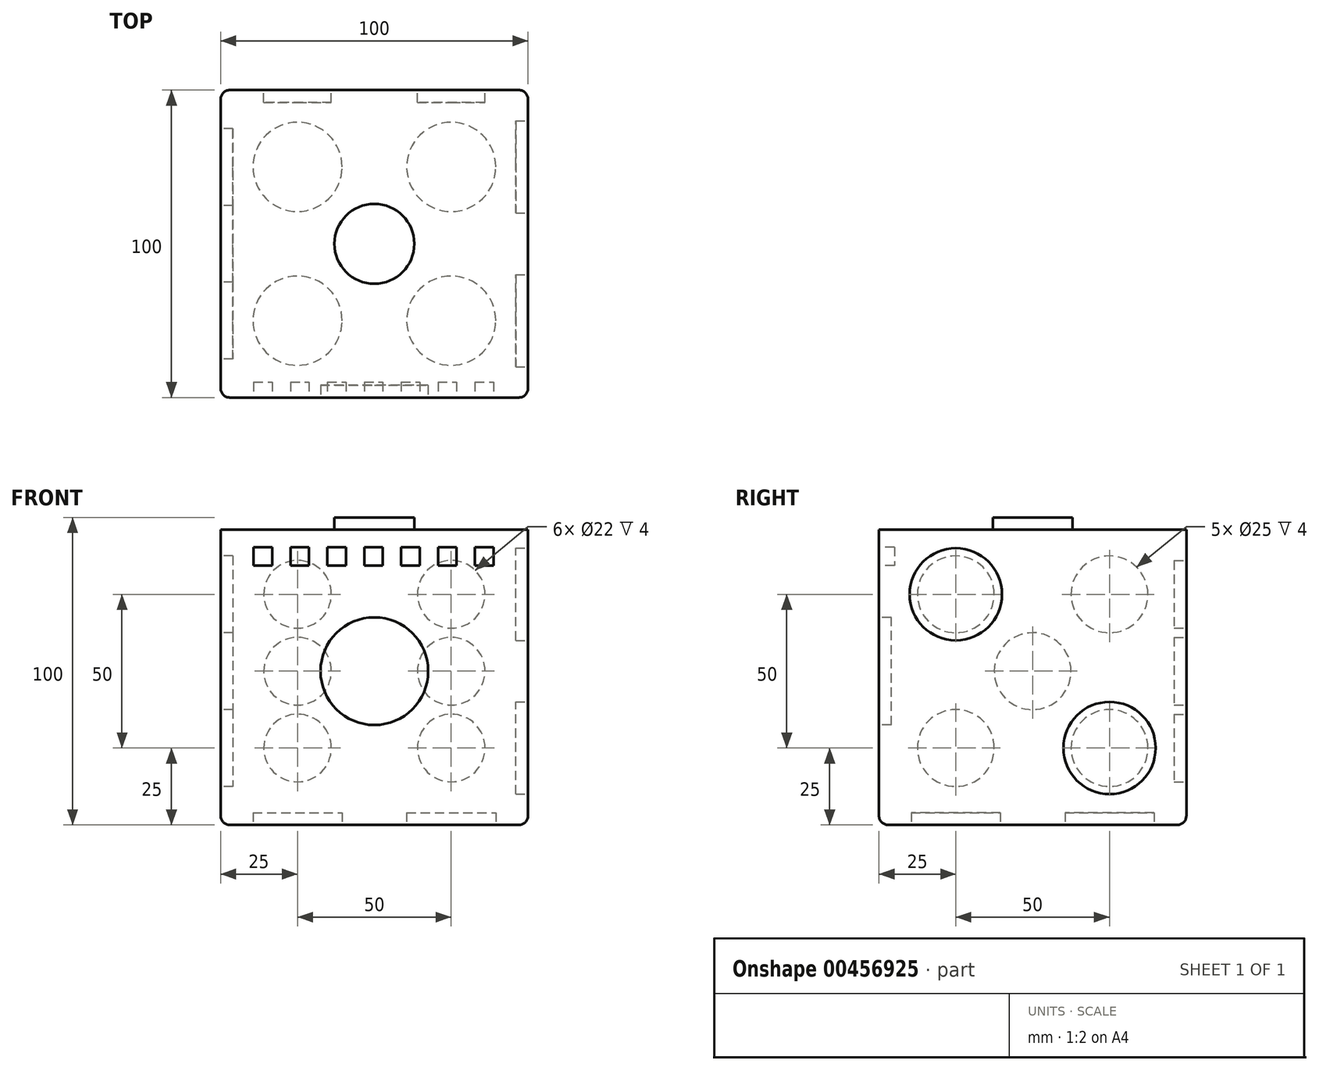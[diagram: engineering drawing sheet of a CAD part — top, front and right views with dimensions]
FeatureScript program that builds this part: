
annotation { "Feature Type Name" : "Feature", "Feature Type Description" : "" }
export const myFeature = defineFeature(function(context is Context, id is Id, definition is map)
    precondition{}
    {
        {
            var Q0;
            Q0=qCreatedBy(makeId("Top.planeOp"),FACE);
            var sketch = newSketch(context, id + "F0", { "sketchPlane" : qUnion([Q0])});
            skLineSegment(sketch, "E0.bottom", {"start": v(50, -50) * mm, "end": v(-50, -50) * mm});
            skLineSegment(sketch, "E0.top", {"start": v(50, 50) * mm, "end": v(-50, 50) * mm});
            skLineSegment(sketch, "E0.left", {"start": v(50, -50) * mm, "end": v(50, 50) * mm});
            skLineSegment(sketch, "E0.right", {"start": v(-50, -50) * mm, "end": v(-50, 50) * mm});
            skPoint(sketch, "E0.middle", {"position": v(0, 0) * mm});
            skSolve(sketch);
        }
        {
            var Q0;
            Q0 = qSketchRegion(id + "F0", true);
            extrude(context, id + "F1", {"entities" : qUnion([Q0]), "endBound" : BoundingType.SYMMETRIC, "depth" : 100 * mm});
        }
        {
            var Q0;
            Q0=makeQuery(id+"F1.opExtrude","SWEPT_FACE",FACE,{"disambiguationData":[OSD([sQuery(id+"F0.wireOp",EDGE,"E0.bottom")])]});
            var sketch = newSketch(context, id + "F2", { "sketchPlane" : qUnion([Q0])});
            skCircle(sketch, "E1", {"center": v(0, 0) * mm, "radius": 17.5 * mm});
            skSolve(sketch);
        }
        {
            var Q0;
            Q0=makeQuery(id+"F2.imprint","IMPRINT",FACE,{"disambiguationData":[TD([[makeQuery(id+"F2.imprint","IMPRINT",EDGE,{"derivedFrom":sQuery(id+"F2.wireOp",EDGE,"E1")}),1.0]])]});
            extrude(context, id + "F3", {"entities" : qUnion([Q0]), "operationType" : NewBodyOperationType.REMOVE, "oppositeDirection" : true, "depth" : 4 * mm});
        }
        {
            var Q0;
            Q0=makeQuery(id+"F1.opExtrude","SWEPT_FACE",FACE,{"disambiguationData":[OSD([sQuery(id+"F0.wireOp",EDGE,"E0.left")])]});
            var sketch = newSketch(context, id + "F4", { "sketchPlane" : qUnion([Q0])});
            skCircle(sketch, "E2", {"center": v(-25, 25) * mm, "radius": 15 * mm});
            skCircle(sketch, "E3", {"center": v(25, -25) * mm, "radius": 15 * mm});
            skSolve(sketch);
        }
        {
            var Q0;
            Q0=makeQuery(id+"F4.imprint","IMPRINT",FACE,{"disambiguationData":[TD([[makeQuery(id+"F4.imprint","IMPRINT",EDGE,{"derivedFrom":sQuery(id+"F4.wireOp",EDGE,"E2")}),1.0]])]});
            var Q1;
            Q1=makeQuery(id+"F4.imprint","IMPRINT",FACE,{"disambiguationData":[TD([[makeQuery(id+"F4.imprint","IMPRINT",EDGE,{"derivedFrom":sQuery(id+"F4.wireOp",EDGE,"E3")}),1.0]])]});
            extrude(context, id + "F5", {"entities" : qUnion([Q0, Q1]), "operationType" : NewBodyOperationType.REMOVE, "oppositeDirection" : true, "depth" : 4 * mm});
        }
        {
            var Q0;
            Q0=makeQuery(id+"F1.opExtrude","CAP_FACE",FACE,{"disambiguationData":[OSD([sQuery(id+"F0.wireOp",EDGE,"E0.bottom"),sQuery(id+"F0.wireOp",EDGE,"E0.top"),sQuery(id+"F0.wireOp",EDGE,"E0.left"),sQuery(id+"F0.wireOp",EDGE,"E0.right")])],"isStart":false});
            var sketch = newSketch(context, id + "F6", { "sketchPlane" : qUnion([Q0])});
            skLineSegment(sketch, "E4", {"start": v(-50, 0) * mm, "end": v(50, 0) * mm});
            skCircle(sketch, "E5", {"center": v(-25, 25) * mm, "radius": 13 * mm});
            skCircle(sketch, "E6", {"center": v(0, 0) * mm, "radius": 13 * mm});
            skCircle(sketch, "E7", {"center": v(25, -25) * mm, "radius": 13 * mm});
            skSolve(sketch);
        }
        {
            var Q0;
            Q0=makeQuery(id+"F6.imprint","IMPRINT",FACE,{"disambiguationData":[TD([[makeQuery(id+"F6.imprint","IMPRINT",EDGE,{"derivedFrom":sQuery(id+"F6.wireOp",EDGE,"E5")}),1.0]])]});
            var Q1;
            {var subQ0=sQuery(id+"F6.wireOp",EDGE,"E6");var subQ1=sQuery(id+"F6.wireOp",EDGE,"E4");var subQ2=makeQuery(id+"F6.imprint","INTERSECT",VERTEX,{"disambiguationData":[OD(0.0)],"derivedFrom":[subQ1,subQ0]});Q1=makeQuery(id+"F6.imprint","IMPRINT",FACE,{"disambiguationData":[TD([[makeQuery(id+"F6.imprint","IMPRINT",EDGE,{"disambiguationData":[TD([[subQ2,-1.0]])],"derivedFrom":subQ1}),1.0]])]});}
            var Q2;
            {var subQ0=sQuery(id+"F6.wireOp",EDGE,"E6");var subQ1=sQuery(id+"F6.wireOp",EDGE,"E4");var subQ2=makeQuery(id+"F6.imprint","INTERSECT",VERTEX,{"disambiguationData":[OD(0.0)],"derivedFrom":[subQ1,subQ0]});Q2=makeQuery(id+"F6.imprint","IMPRINT",FACE,{"disambiguationData":[TD([[makeQuery(id+"F6.imprint","IMPRINT",EDGE,{"disambiguationData":[TD([[subQ2,-1.0]])],"derivedFrom":subQ1}),-1.0]])]});}
            var Q3;
            Q3=makeQuery(id+"F6.imprint","IMPRINT",FACE,{"disambiguationData":[TD([[makeQuery(id+"F6.imprint","IMPRINT",EDGE,{"derivedFrom":sQuery(id+"F6.wireOp",EDGE,"E7")}),1.0]])]});
            extrude(context, id + "F7", {"entities" : qUnion([Q0, Q1, Q2, Q3]), "operationType" : NewBodyOperationType.REMOVE, "oppositeDirection" : true, "depth" : 4 * mm});
        }
        {
            var Q0;
            Q0=makeQuery(id+"F1.opExtrude","CAP_FACE",FACE,{"disambiguationData":[OSD([sQuery(id+"F0.wireOp",EDGE,"E0.bottom"),sQuery(id+"F0.wireOp",EDGE,"E0.top"),sQuery(id+"F0.wireOp",EDGE,"E0.left"),sQuery(id+"F0.wireOp",EDGE,"E0.right")])],"isStart":true});
            var sketch = newSketch(context, id + "F8", { "sketchPlane" : qUnion([Q0])});
            skCircle(sketch, "E8", {"center": v(-25, -25) * mm, "radius": 14.5 * mm});
            skCircle(sketch, "E9", {"center": v(25, -25) * mm, "radius": 14.5 * mm});
            skCircle(sketch, "E10", {"center": v(25, 25) * mm, "radius": 14.5 * mm});
            skCircle(sketch, "E11", {"center": v(-25, 25) * mm, "radius": 14.5 * mm});
            skSolve(sketch);
        }
        {
            var Q0;
            Q0=makeQuery(id+"F8.imprint","IMPRINT",FACE,{"disambiguationData":[TD([[makeQuery(id+"F8.imprint","IMPRINT",EDGE,{"derivedFrom":sQuery(id+"F8.wireOp",EDGE,"E11")}),1.0]])]});
            var Q1;
            Q1=makeQuery(id+"F8.imprint","IMPRINT",FACE,{"disambiguationData":[TD([[makeQuery(id+"F8.imprint","IMPRINT",EDGE,{"derivedFrom":sQuery(id+"F8.wireOp",EDGE,"E10")}),1.0]])]});
            var Q2;
            Q2=makeQuery(id+"F8.imprint","IMPRINT",FACE,{"disambiguationData":[TD([[makeQuery(id+"F8.imprint","IMPRINT",EDGE,{"derivedFrom":sQuery(id+"F8.wireOp",EDGE,"E8")}),1.0]])]});
            var Q3;
            Q3=makeQuery(id+"F8.imprint","IMPRINT",FACE,{"disambiguationData":[TD([[makeQuery(id+"F8.imprint","IMPRINT",EDGE,{"derivedFrom":sQuery(id+"F8.wireOp",EDGE,"E9")}),1.0]])]});
            extrude(context, id + "F9", {"entities" : qUnion([Q0, Q1, Q2, Q3]), "operationType" : NewBodyOperationType.REMOVE, "oppositeDirection" : true, "depth" : 4 * mm});
        }
        {
            var Q0;
            Q0=makeQuery(id+"F1.opExtrude","SWEPT_FACE",FACE,{"disambiguationData":[OSD([sQuery(id+"F0.wireOp",EDGE,"E0.right")])]});
            var sketch = newSketch(context, id + "F10", { "sketchPlane" : qUnion([Q0])});
            skCircle(sketch, "E12", {"center": v(0, 0) * mm, "radius": 12.5 * mm});
            skCircle(sketch, "E13", {"center": v(25, 25) * mm, "radius": 12.5 * mm});
            skCircle(sketch, "E14", {"center": v(-25, 25) * mm, "radius": 12.5 * mm});
            skCircle(sketch, "E15", {"center": v(-25, -25) * mm, "radius": 12.5 * mm});
            skCircle(sketch, "E16", {"center": v(25, -25) * mm, "radius": 12.5 * mm});
            skSolve(sketch);
        }
        {
            var Q0;
            Q0 = qSketchRegion(id + "F10", true);
            extrude(context, id + "F11", {"entities" : qUnion([Q0]), "operationType" : NewBodyOperationType.REMOVE, "oppositeDirection" : true, "depth" : 4 * mm});
        }
        {
            var Q0;
            Q0=makeQuery(id+"F1.opExtrude","SWEPT_FACE",FACE,{"disambiguationData":[OSD([sQuery(id+"F0.wireOp",EDGE,"E0.top")])]});
            var sketch = newSketch(context, id + "F12", { "sketchPlane" : qUnion([Q0])});
            skCircle(sketch, "E17", {"center": v(-25, 0) * mm, "radius": 11 * mm});
            skCircle(sketch, "E18", {"center": v(-25, 25) * mm, "radius": 11 * mm});
            skCircle(sketch, "E19", {"center": v(-25, -25) * mm, "radius": 11 * mm});
            skCircle(sketch, "E20", {"center": v(25, -25) * mm, "radius": 11 * mm});
            skCircle(sketch, "E21", {"center": v(25, 0) * mm, "radius": 11 * mm});
            skCircle(sketch, "E22", {"center": v(25, 25) * mm, "radius": 11 * mm});
            skSolve(sketch);
        }
        {
            var Q0;
            Q0 = qSketchRegion(id + "F12", true);
            extrude(context, id + "F13", {"entities" : qUnion([Q0]), "operationType" : NewBodyOperationType.REMOVE, "oppositeDirection" : true, "depth" : 4 * mm});
        }
        {
            var Q0;
            Q0=makeQuery(id+"F1.opExtrude","CAP_EDGE",EDGE,{"disambiguationData":[OSD([sQuery(id+"F0.wireOp",EDGE,"E0.left")])],"isStart":false});
            var Q1;
            Q1=makeQuery(id+"F1.opExtrude","CAP_EDGE",EDGE,{"disambiguationData":[OSD([sQuery(id+"F0.wireOp",EDGE,"E0.top")])],"isStart":false});
            var Q2;
            Q2=makeQuery(id+"F1.opExtrude","CAP_EDGE",EDGE,{"disambiguationData":[OSD([sQuery(id+"F0.wireOp",EDGE,"E0.right")])],"isStart":false});
            var Q3;
            Q3=makeQuery(id+"F1.opExtrude","CAP_EDGE",EDGE,{"disambiguationData":[OSD([sQuery(id+"F0.wireOp",EDGE,"E0.bottom")])],"isStart":false});
            var Q4;
            Q4=makeQuery(id+"F1.opExtrude","SWEPT_EDGE",EDGE,{"disambiguationData":[OSD([sQuery(id+"F0.wireOp",EDGE,"E0.bottom"),sQuery(id+"F0.wireOp",EDGE,"E0.right")])]});
            var Q5;
            Q5=makeQuery(id+"F1.opExtrude","CAP_EDGE",EDGE,{"disambiguationData":[OSD([sQuery(id+"F0.wireOp",EDGE,"E0.bottom")])],"isStart":true});
            var Q6;
            Q6=makeQuery(id+"F1.opExtrude","SWEPT_EDGE",EDGE,{"disambiguationData":[OSD([sQuery(id+"F0.wireOp",EDGE,"E0.bottom"),sQuery(id+"F0.wireOp",EDGE,"E0.left")])]});
            var Q7;
            Q7=makeQuery(id+"F1.opExtrude","CAP_EDGE",EDGE,{"disambiguationData":[OSD([sQuery(id+"F0.wireOp",EDGE,"E0.left")])],"isStart":true});
            var Q8;
            Q8=makeQuery(id+"F1.opExtrude","CAP_EDGE",EDGE,{"disambiguationData":[OSD([sQuery(id+"F0.wireOp",EDGE,"E0.top")])],"isStart":true});
            var Q9;
            Q9=makeQuery(id+"F1.opExtrude","SWEPT_EDGE",EDGE,{"disambiguationData":[OSD([sQuery(id+"F0.wireOp",EDGE,"E0.top"),sQuery(id+"F0.wireOp",EDGE,"E0.left")])]});
            var Q10;
            Q10=makeQuery(id+"F1.opExtrude","SWEPT_EDGE",EDGE,{"disambiguationData":[OSD([sQuery(id+"F0.wireOp",EDGE,"E0.top"),sQuery(id+"F0.wireOp",EDGE,"E0.right")])]});
            var Q11;
            Q11=makeQuery(id+"F1.opExtrude","CAP_EDGE",EDGE,{"disambiguationData":[OSD([sQuery(id+"F0.wireOp",EDGE,"E0.right")])],"isStart":true});
            fillet(context, id + "F14", {"entities" : qUnion([Q0, Q1, Q2, Q3, Q4, Q5, Q6, Q7, Q8, Q9, Q10, Q11]), "radius" : 3 * mm, "tangentPropagation" : true, "allowEdgeOverflow" : false});
        }
        {
            var Q0;
            Q0=makeQuery(id+"F1.opExtrude","SWEPT_FACE",FACE,{"disambiguationData":[OSD([sQuery(id+"F0.wireOp",EDGE,"E0.bottom")])]});
            var sketch = newSketch(context, id + "F15", { "sketchPlane" : qUnion([Q0])});
            skLineSegment(sketch, "E23.bottom", {"start": v(-39.26, 40.35) * mm, "end": v(-33.26, 40.35) * mm});
            skLineSegment(sketch, "E23.top", {"start": v(-39.26, 34.35) * mm, "end": v(-33.26, 34.35) * mm});
            skLineSegment(sketch, "E23.left", {"start": v(-39.26, 40.35) * mm, "end": v(-39.26, 34.35) * mm});
            skLineSegment(sketch, "E23.right", {"start": v(-33.26, 40.35) * mm, "end": v(-33.26, 34.35) * mm});
            skLineSegment(sketch, "E24.1.0.0", {"start": v(-27.26, 40.35) * mm, "end": v(-21.26, 40.35) * mm});
            skLineSegment(sketch, "E24.1.0.1", {"start": v(-21.26, 40.35) * mm, "end": v(-21.26, 34.35) * mm});
            skLineSegment(sketch, "E24.1.0.2", {"start": v(-27.26, 34.35) * mm, "end": v(-21.26, 34.35) * mm});
            skLineSegment(sketch, "E24.1.0.3", {"start": v(-27.26, 40.35) * mm, "end": v(-27.26, 34.35) * mm});
            skLineSegment(sketch, "E24.2.0.0", {"start": v(-15.26, 40.35) * mm, "end": v(-9.26, 40.35) * mm});
            skLineSegment(sketch, "E24.2.0.1", {"start": v(-9.26, 40.35) * mm, "end": v(-9.26, 34.35) * mm});
            skLineSegment(sketch, "E24.2.0.2", {"start": v(-15.26, 34.35) * mm, "end": v(-9.26, 34.35) * mm});
            skLineSegment(sketch, "E24.2.0.3", {"start": v(-15.26, 40.35) * mm, "end": v(-15.26, 34.35) * mm});
            skLineSegment(sketch, "E24.direction1", {"start": v(-39.26, 34.35) * mm, "end": v(-27.26, 34.35) * mm, "construction": true});
            skLineSegment(sketch, "E25.0.3.0", {"start": v(-3.26, 40.35) * mm, "end": v(2.74, 40.35) * mm});
            skLineSegment(sketch, "E25.3.3.0", {"start": v(2.74, 40.35) * mm, "end": v(2.74, 34.35) * mm});
            skLineSegment(sketch, "E25.6.3.0", {"start": v(-3.26, 34.35) * mm, "end": v(2.74, 34.35) * mm});
            skLineSegment(sketch, "E25.9.3.0", {"start": v(-3.26, 40.35) * mm, "end": v(-3.26, 34.35) * mm});
            skLineSegment(sketch, "E25.0.4.0", {"start": v(8.74, 40.35) * mm, "end": v(14.74, 40.35) * mm});
            skLineSegment(sketch, "E25.3.4.0", {"start": v(14.74, 40.35) * mm, "end": v(14.74, 34.35) * mm});
            skLineSegment(sketch, "E25.6.4.0", {"start": v(8.74, 34.35) * mm, "end": v(14.74, 34.35) * mm});
            skLineSegment(sketch, "E25.9.4.0", {"start": v(8.74, 40.35) * mm, "end": v(8.74, 34.35) * mm});
            skLineSegment(sketch, "E25.0.5.0", {"start": v(20.74, 40.35) * mm, "end": v(26.74, 40.35) * mm});
            skLineSegment(sketch, "E25.3.5.0", {"start": v(26.74, 40.35) * mm, "end": v(26.74, 34.35) * mm});
            skLineSegment(sketch, "E25.6.5.0", {"start": v(20.74, 34.35) * mm, "end": v(26.74, 34.35) * mm});
            skLineSegment(sketch, "E25.9.5.0", {"start": v(20.74, 40.35) * mm, "end": v(20.74, 34.35) * mm});
            skLineSegment(sketch, "E25.0.6.0", {"start": v(32.74, 40.35) * mm, "end": v(38.74, 40.35) * mm});
            skLineSegment(sketch, "E25.3.6.0", {"start": v(38.74, 40.35) * mm, "end": v(38.74, 34.35) * mm});
            skLineSegment(sketch, "E25.6.6.0", {"start": v(32.74, 34.35) * mm, "end": v(38.74, 34.35) * mm});
            skLineSegment(sketch, "E25.9.6.0", {"start": v(32.74, 40.35) * mm, "end": v(32.74, 34.35) * mm});
            skLineSegment(sketch, "E26", {"start": v(-47, 0) * mm, "end": v(47, 0) * mm});
            skLineSegment(sketch, "E27.MirrorCS", {"start": v(32.74, -34.35) * mm, "end": v(38.74, -34.35) * mm});
            skLineSegment(sketch, "E28.MirrorCS", {"start": v(32.74, -40.35) * mm, "end": v(38.74, -40.35) * mm});
            skLineSegment(sketch, "E29.MirrorCS", {"start": v(-39.26, -34.35) * mm, "end": v(-33.26, -34.35) * mm});
            skLineSegment(sketch, "E30.MirrorCS", {"start": v(-15.26, -40.35) * mm, "end": v(-15.26, -34.35) * mm});
            skLineSegment(sketch, "E31.MirrorCS", {"start": v(-39.26, -40.35) * mm, "end": v(-33.26, -40.35) * mm});
            skLineSegment(sketch, "E32.MirrorCS", {"start": v(8.74, -40.35) * mm, "end": v(14.74, -40.35) * mm});
            skLineSegment(sketch, "E33.MirrorCS", {"start": v(-39.26, -34.35) * mm, "end": v(-27.26, -34.35) * mm, "construction": true});
            skLineSegment(sketch, "E34.MirrorCS", {"start": v(-27.26, -40.35) * mm, "end": v(-21.26, -40.35) * mm});
            skLineSegment(sketch, "E35.MirrorCS", {"start": v(20.74, -34.35) * mm, "end": v(26.74, -34.35) * mm});
            skLineSegment(sketch, "E36.MirrorCS", {"start": v(20.74, -40.35) * mm, "end": v(26.74, -40.35) * mm});
            skLineSegment(sketch, "E37.MirrorCS", {"start": v(-15.26, -40.35) * mm, "end": v(-9.26, -40.35) * mm});
            skLineSegment(sketch, "E38.MirrorCS", {"start": v(32.74, -40.35) * mm, "end": v(32.74, -34.35) * mm});
            skLineSegment(sketch, "E39.MirrorCS", {"start": v(20.74, -40.35) * mm, "end": v(20.74, -34.35) * mm});
            skLineSegment(sketch, "E40.MirrorCS", {"start": v(-9.26, -40.35) * mm, "end": v(-9.26, -34.35) * mm});
            skLineSegment(sketch, "E41.MirrorCS", {"start": v(26.74, -40.35) * mm, "end": v(26.74, -34.35) * mm});
            skLineSegment(sketch, "E42.MirrorCS", {"start": v(14.74, -40.35) * mm, "end": v(14.74, -34.35) * mm});
            skLineSegment(sketch, "E43.MirrorCS", {"start": v(-3.26, -40.35) * mm, "end": v(-3.26, -34.35) * mm});
            skLineSegment(sketch, "E44.MirrorCS", {"start": v(2.74, -40.35) * mm, "end": v(2.74, -34.35) * mm});
            skLineSegment(sketch, "E45.MirrorCS", {"start": v(8.74, -40.35) * mm, "end": v(8.74, -34.35) * mm});
            skLineSegment(sketch, "E46.MirrorCS", {"start": v(-27.26, -40.35) * mm, "end": v(-27.26, -34.35) * mm});
            skLineSegment(sketch, "E47.MirrorCS", {"start": v(-27.26, -34.35) * mm, "end": v(-21.26, -34.35) * mm});
            skLineSegment(sketch, "E48.MirrorCS", {"start": v(-21.26, -40.35) * mm, "end": v(-21.26, -34.35) * mm});
            skLineSegment(sketch, "E49.MirrorCS", {"start": v(-33.26, -40.35) * mm, "end": v(-33.26, -34.35) * mm});
            skLineSegment(sketch, "E50.MirrorCS", {"start": v(-39.26, -40.35) * mm, "end": v(-39.26, -34.35) * mm});
            skLineSegment(sketch, "E51.MirrorCS", {"start": v(38.74, -40.35) * mm, "end": v(38.74, -34.35) * mm});
            skLineSegment(sketch, "E52.MirrorCS", {"start": v(-3.26, -40.35) * mm, "end": v(2.74, -40.35) * mm});
            skLineSegment(sketch, "E53.MirrorCS", {"start": v(-3.26, -34.35) * mm, "end": v(2.74, -34.35) * mm});
            skLineSegment(sketch, "E54.MirrorCS", {"start": v(-15.26, -34.35) * mm, "end": v(-9.26, -34.35) * mm});
            skLineSegment(sketch, "E55.MirrorCS", {"start": v(8.74, -34.35) * mm, "end": v(14.74, -34.35) * mm});
            skSolve(sketch);
        }
        {
            var Q0;
            Q0=makeQuery(id+"F15.imprint","IMPRINT",FACE,{"disambiguationData":[TD([[makeQuery(id+"F15.imprint","IMPRINT",EDGE,{"derivedFrom":sQuery(id+"F15.wireOp",EDGE,"E23.bottom")}),-1.0]])]});
            var Q1;
            Q1=makeQuery(id+"F15.imprint","IMPRINT",FACE,{"disambiguationData":[TD([[makeQuery(id+"F15.imprint","IMPRINT",EDGE,{"derivedFrom":sQuery(id+"F15.wireOp",EDGE,"E24.1.0.0")}),-1.0]])]});
            var Q2;
            Q2=makeQuery(id+"F15.imprint","IMPRINT",FACE,{"disambiguationData":[TD([[makeQuery(id+"F15.imprint","IMPRINT",EDGE,{"derivedFrom":sQuery(id+"F15.wireOp",EDGE,"E24.2.0.0")}),-1.0]])]});
            var Q3;
            Q3=makeQuery(id+"F15.imprint","IMPRINT",FACE,{"disambiguationData":[TD([[makeQuery(id+"F15.imprint","IMPRINT",EDGE,{"derivedFrom":sQuery(id+"F15.wireOp",EDGE,"E25.0.3.0")}),-1.0]])]});
            var Q4;
            Q4=makeQuery(id+"F15.imprint","IMPRINT",FACE,{"disambiguationData":[TD([[makeQuery(id+"F15.imprint","IMPRINT",EDGE,{"derivedFrom":sQuery(id+"F15.wireOp",EDGE,"E25.0.4.0")}),-1.0]])]});
            var Q5;
            Q5=makeQuery(id+"F15.imprint","IMPRINT",FACE,{"disambiguationData":[TD([[makeQuery(id+"F15.imprint","IMPRINT",EDGE,{"derivedFrom":sQuery(id+"F15.wireOp",EDGE,"E25.0.5.0")}),-1.0]])]});
            var Q6;
            Q6=makeQuery(id+"F15.imprint","IMPRINT",FACE,{"disambiguationData":[TD([[makeQuery(id+"F15.imprint","IMPRINT",EDGE,{"derivedFrom":sQuery(id+"F15.wireOp",EDGE,"E25.0.6.0")}),-1.0]])]});
            extrude(context, id + "F16", {"entities" : qUnion([Q0, Q1, Q2, Q3, Q4, Q5, Q6]), "operationType" : NewBodyOperationType.REMOVE, "oppositeDirection" : true, "depth" : 5 * mm});
        }
    });
